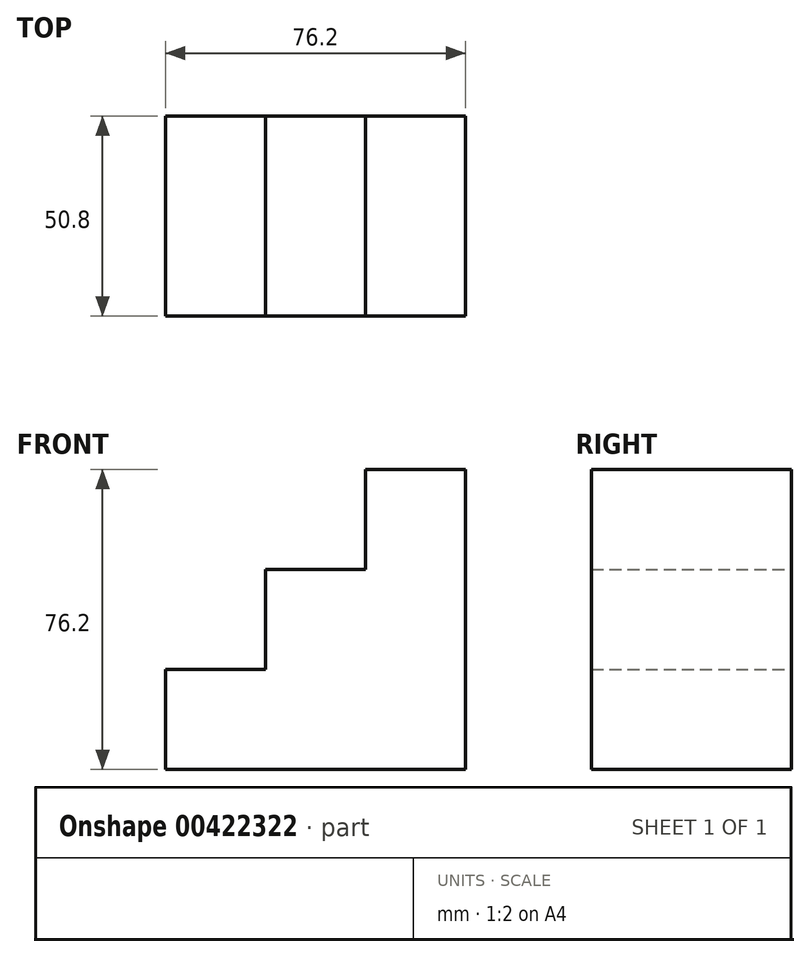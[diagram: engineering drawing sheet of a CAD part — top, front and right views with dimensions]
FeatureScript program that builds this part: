
annotation { "Feature Type Name" : "Feature", "Feature Type Description" : "" }
export const myFeature = defineFeature(function(context is Context, id is Id, definition is map)
    precondition{}
    {
        {
            var Q0;
            Q0=qCreatedBy(makeId("Front.planeOp"),FACE);
            var sketch = newSketch(context, id + "F0", { "sketchPlane" : qUnion([Q0])});
            skLineSegment(sketch, "E0", {"start": v(-62.4, -67.6) * mm, "end": v(13.8, -67.6) * mm});
            skLineSegment(sketch, "E1", {"start": v(13.8, -67.6) * mm, "end": v(13.8, 8.6) * mm});
            skLineSegment(sketch, "E2", {"start": v(13.8, 8.6) * mm, "end": v(-11.6, 8.6) * mm});
            skLineSegment(sketch, "E3", {"start": v(-11.6, 8.6) * mm, "end": v(-11.6, -16.8) * mm});
            skLineSegment(sketch, "E4", {"start": v(-11.6, -16.8) * mm, "end": v(-37, -16.8) * mm});
            skLineSegment(sketch, "E5", {"start": v(-37, -16.8) * mm, "end": v(-37, -42.2) * mm});
            skLineSegment(sketch, "E6", {"start": v(-37, -42.2) * mm, "end": v(-62.4, -42.2) * mm});
            skLineSegment(sketch, "E7", {"start": v(-62.4, -42.2) * mm, "end": v(-62.4, -67.6) * mm});
            skSolve(sketch);
        }
        {
            var Q0;
            Q0=makeQuery(id+"F0.imprint","IMPRINT",FACE,{"disambiguationData":[TD([[makeQuery(id+"F0.imprint","IMPRINT",EDGE,{"derivedFrom":sQuery(id+"F0.wireOp",EDGE,"E0")}),1.0]])]});
            extrude(context, id + "F1", {"entities" : qUnion([Q0]), "depth" : 50.8 * mm});
        }
    });
